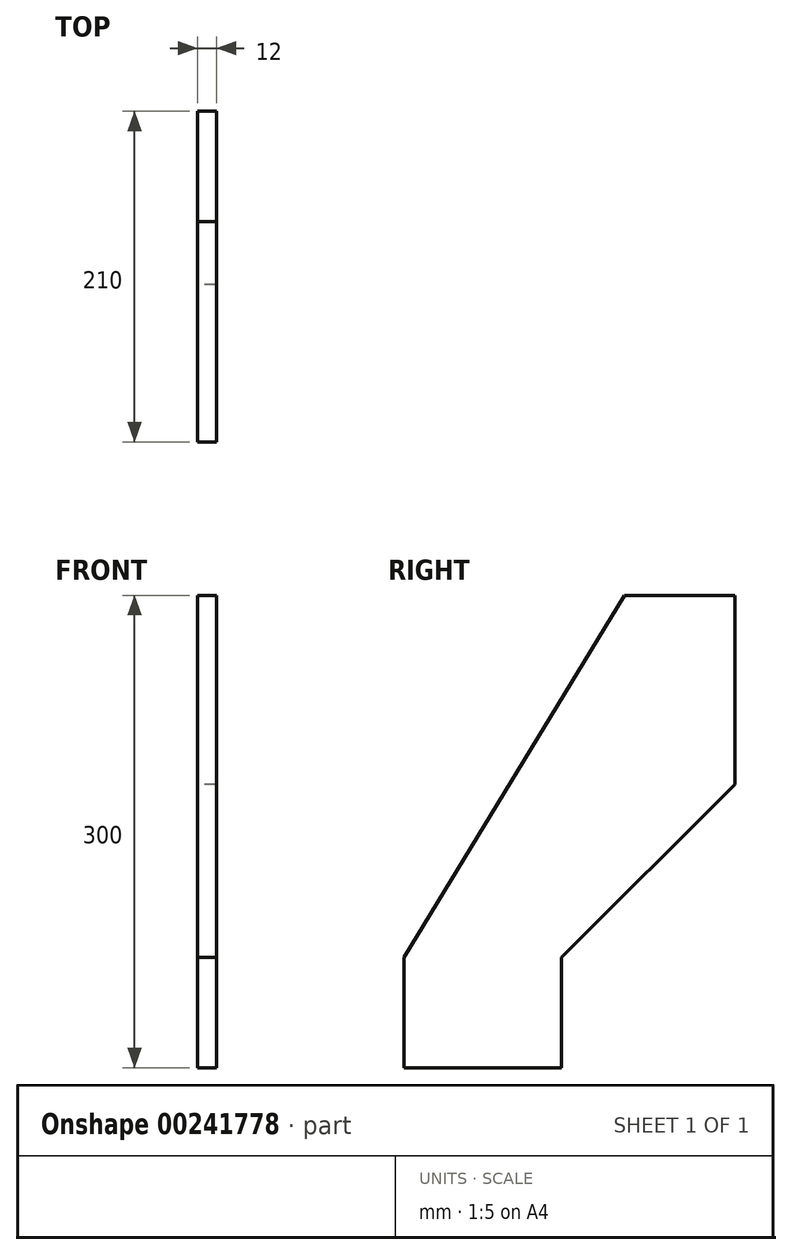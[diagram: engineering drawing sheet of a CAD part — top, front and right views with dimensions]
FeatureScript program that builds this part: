
annotation { "Feature Type Name" : "Feature", "Feature Type Description" : "" }
export const myFeature = defineFeature(function(context is Context, id is Id, definition is map)
    precondition{}
    {
        {
            var Q0;
            Q0=qCreatedBy(makeId("Right.planeOp"),FACE);
            var sketch = newSketch(context, id + "F0", { "sketchPlane" : qUnion([Q0])});
            skLineSegment(sketch, "E0.bottom", {"start": v(148.17, 153.66) * mm, "end": v(218.17, 153.66) * mm});
            skLineSegment(sketch, "E0.top", {"start": v(8.17, -146.34) * mm, "end": v(108.17, -146.34) * mm});
            skLineSegment(sketch, "E0.left", {"start": v(8.17, -76.34) * mm, "end": v(8.17, -146.34) * mm});
            skLineSegment(sketch, "E0.right", {"start": v(218.17, 153.66) * mm, "end": v(218.17, 33.66) * mm});
            skPoint(sketch, "E1", {"position": v(148.17, 153.66) * mm});
            skPoint(sketch, "E2", {"position": v(8.17, -76.34) * mm});
            skLineSegment(sketch, "E3", {"start": v(148.17, 153.66) * mm, "end": v(8.17, -76.34) * mm});
            skPoint(sketch, "E4", {"position": v(218.17, 33.66) * mm});
            skLineSegment(sketch, "E5", {"start": v(218.17, 33.66) * mm, "end": v(108.17, -76.34) * mm});
            skLineSegment(sketch, "E6", {"start": v(108.17, -146.34) * mm, "end": v(108.17, -76.34) * mm});
            skSolve(sketch);
        }
        {
            var Q0;
            Q0=makeQuery(id+"F0.imprint","IMPRINT",FACE,{"disambiguationData":[TD([[makeQuery(id+"F0.imprint","IMPRINT",EDGE,{"derivedFrom":sQuery(id+"F0.wireOp",EDGE,"E0.bottom")}),-1.0]])]});
            extrude(context, id + "F1", {"entities" : qUnion([Q0]), "depth" : 12 * mm});
        }
    });
